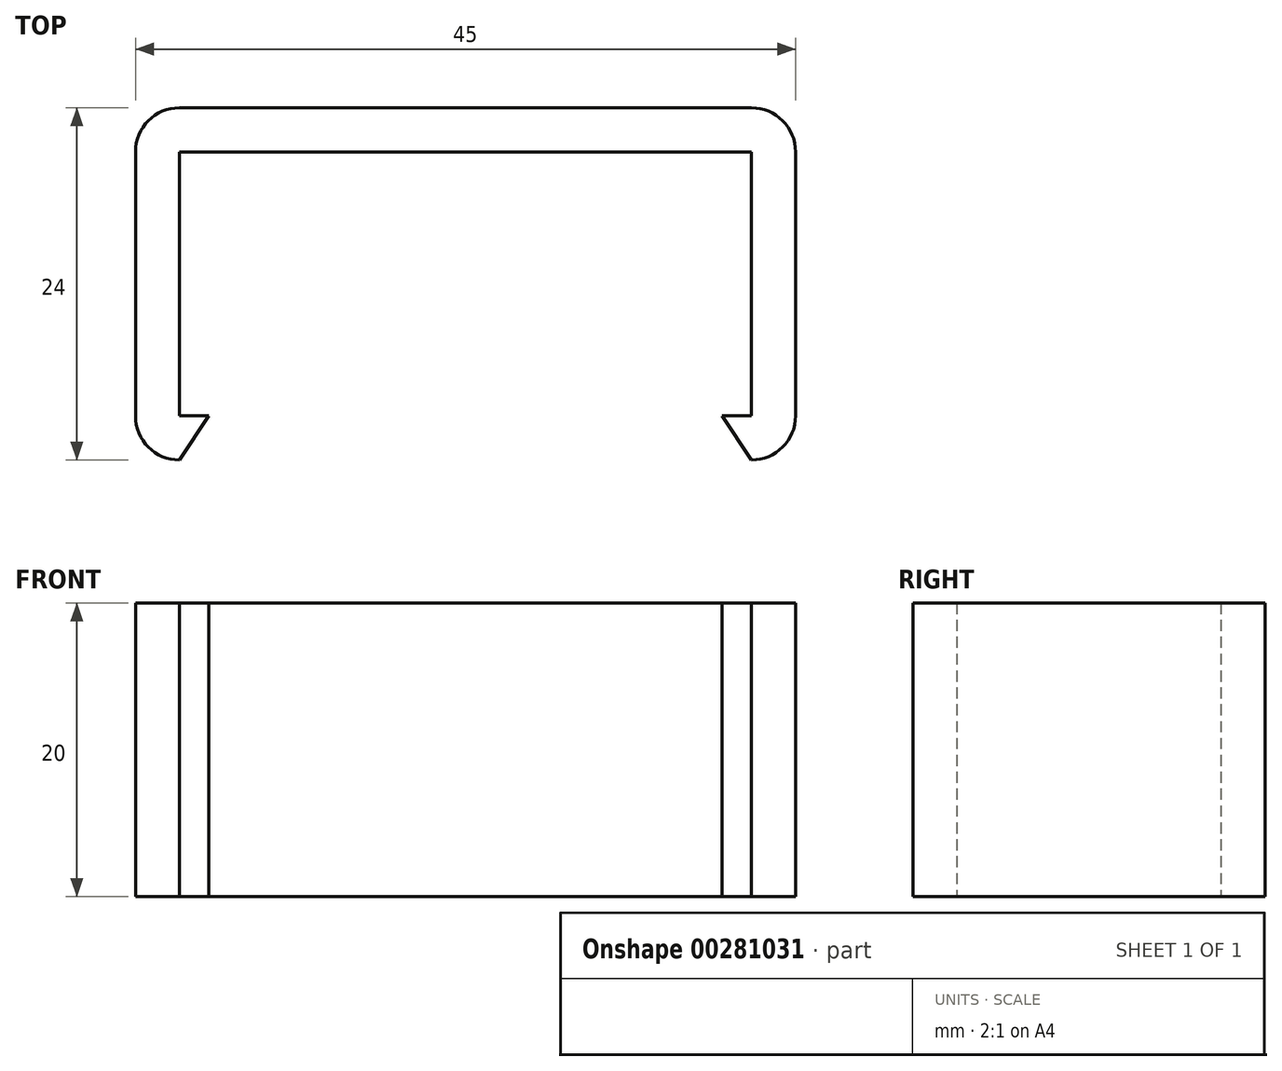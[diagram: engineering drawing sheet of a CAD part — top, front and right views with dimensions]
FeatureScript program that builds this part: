
annotation { "Feature Type Name" : "Feature", "Feature Type Description" : "" }
export const myFeature = defineFeature(function(context is Context, id is Id, definition is map)
    precondition{}
    {
        {
            var Q0;
            Q0=qCreatedBy(makeId("Front.planeOp"),FACE);
            var sketch = newSketch(context, id + "F0", { "sketchPlane" : qUnion([Q0])});
            skLineSegment(sketch, "E0.bottom", {"start": v(-22.5, 24) * mm, "end": v(22.5, 24) * mm});
            skLineSegment(sketch, "E0.top", {"start": v(-22.5, 0) * mm, "end": v(22.5, 0) * mm});
            skLineSegment(sketch, "E0.left", {"start": v(-22.5, 24) * mm, "end": v(-22.5, 0) * mm});
            skLineSegment(sketch, "E0.right", {"start": v(22.5, 24) * mm, "end": v(22.5, 0) * mm});
            skLineSegment(sketch, "E1.bottom", {"start": v(-19.5, 21) * mm, "end": v(19.5, 21) * mm});
            skLineSegment(sketch, "E1.top", {"start": v(-19.5, 3) * mm, "end": v(19.5, 3) * mm});
            skLineSegment(sketch, "E1.left", {"start": v(-19.5, 21) * mm, "end": v(-19.5, 3) * mm});
            skLineSegment(sketch, "E1.right", {"start": v(19.5, 21) * mm, "end": v(19.5, 3) * mm});
            skLineSegment(sketch, "E2", {"start": v(-17.5, 3) * mm, "end": v(-19.5, 0) * mm});
            skLineSegment(sketch, "E3", {"start": v(17.5, 3) * mm, "end": v(19.5, 0) * mm});
            skSolve(sketch);
        }
        {
            var Q0;
            Q0=makeQuery(id+"F0.imprint","IMPRINT",FACE,{"disambiguationData":[TD([[makeQuery(id+"F0.imprint","IMPRINT",EDGE,{"derivedFrom":sQuery(id+"F0.wireOp",EDGE,"E0.bottom")}),-1.0]])]});
            extrude(context, id + "F1", {"entities" : qUnion([Q0]), "depth" : 20 * mm});
        }
        {
            var Q0;
            Q0=makeQuery(id+"F1.opExtrude","SWEPT_BODY",BODY,{"disambiguationData":[OSD([sQuery(id+"F0.wireOp",EDGE,"E0.bottom"),sQuery(id+"F0.wireOp",EDGE,"E0.top"),sQuery(id+"F0.wireOp",EDGE,"E0.left"),sQuery(id+"F0.wireOp",EDGE,"E0.right"),sQuery(id+"F0.wireOp",EDGE,"E1.bottom"),sQuery(id+"F0.wireOp",EDGE,"E1.top"),sQuery(id+"F0.wireOp",EDGE,"E1.left"),sQuery(id+"F0.wireOp",EDGE,"E1.right"),sQuery(id+"F0.wireOp",EDGE,"E2"),sQuery(id+"F0.wireOp",EDGE,"E3")])]});
            var Q1;
            Q1=makeQuery(id+"F1.opExtrude","CAP_EDGE",EDGE,{"disambiguationData":[OSD([sQuery(id+"F0.wireOp",EDGE,"E0.bottom")])],"isStart":false});
            transform(context, id + "F2", {"entities" : qUnion([Q0]), "transformType" : TransformType.ROTATION, "transformAxis" : qUnion([Q1]), "angle" : 270 * degree, "makeCopy" : false});
        }
        {
            var Q0;
            Q0=makeQuery(id+"F1.opExtrude","SWEPT_EDGE",EDGE,{"disambiguationData":[OSD([sQuery(id+"F0.wireOp",EDGE,"E0.bottom"),sQuery(id+"F0.wireOp",EDGE,"E0.left")])]});
            var Q1;
            Q1=makeQuery(id+"F1.opExtrude","SWEPT_EDGE",EDGE,{"disambiguationData":[OSD([sQuery(id+"F0.wireOp",EDGE,"E0.top"),sQuery(id+"F0.wireOp",EDGE,"E0.left")])]});
            var Q2;
            Q2=makeQuery(id+"F1.opExtrude","SWEPT_EDGE",EDGE,{"disambiguationData":[OSD([sQuery(id+"F0.wireOp",EDGE,"E0.top"),sQuery(id+"F0.wireOp",EDGE,"E0.right")])]});
            var Q3;
            Q3=makeQuery(id+"F1.opExtrude","SWEPT_EDGE",EDGE,{"disambiguationData":[OSD([sQuery(id+"F0.wireOp",EDGE,"E0.bottom"),sQuery(id+"F0.wireOp",EDGE,"E0.right")])]});
            fillet(context, id + "F3", {"entities" : qUnion([Q0, Q1, Q2, Q3]), "radius" : 3 * mm, "tangentPropagation" : true, "allowEdgeOverflow" : false});
        }
    });
